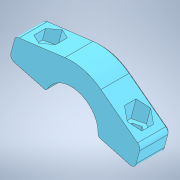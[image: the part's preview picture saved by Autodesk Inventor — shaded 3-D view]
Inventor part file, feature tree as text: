
AUTODESK INVENTOR PART (.ipt)
format: ipt  version: 2021.2 (Build 252289000, 289)  size: 264,704 bytes
history: native  units: mm
features: other x4, fillet x1, chamfer x1
ambient origin geometry x8: Origin, YZ Plane, XZ Plane, XY Plane, X Axis, Y Axis, Z Axis, Center Point
bodies: Body1 (feature_tree)
feature tree (6):
  other  "Твёрдое тело.ipt"
  fillet  "Сопряжение2"  Radius=10.0mm
  chamfer  "Фаска2"  Distance=1.0mm
  other  "Скобка 1::Твёрдое тело.ipt"
  other  "Элемент создания тегов1"
  other  "Твердое тело1"
